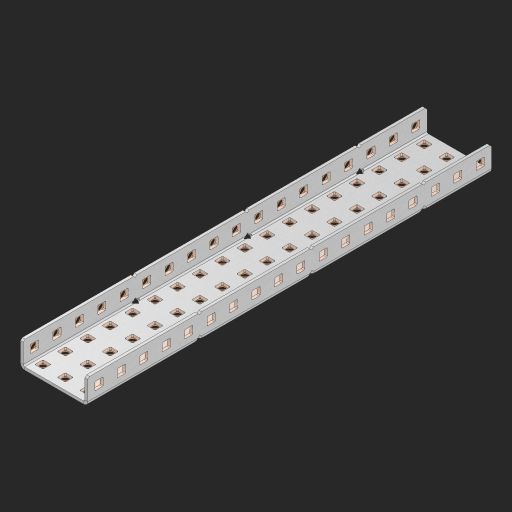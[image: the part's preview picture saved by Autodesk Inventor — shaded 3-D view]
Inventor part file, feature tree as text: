
AUTODESK INVENTOR PART (.ipt)
format: ipt  version: 2023 (Build 270158000, 158)  size: 1,276,928 bytes
history: native  units: in
note: dims shown in document units (in); Inventor stores cm internally (conversion verified against a paired STEP export)
features: other x95, extrude x89, sheet_metal_op x10, sketch x8, mirror x1, pattern_linear x1, chamfer x1
ambient origin geometry x8: Origin, YZ Plane, XZ Plane, XY Plane, X Axis, Y Axis, Z Axis, Center Point
bodies: Solid1 (feature_tree), Body (feature_tree)
feature tree (205):
  other  "Flange Pattern Plane"
  sheet_metal_op  "Flange Pattern"
  sheet_metal_op  "Body Pattern"
  other  "Arc Length"
  mirror  "Notch Mirror"
  pattern_linear  "Notch Pattern"  Spacing1=0.25in  [1 undecoded]
  chamfer  "End Chamfer"
  extrude  "Half Cut"  Depth=0.0625in
  sketch  "Sketch1"  dims[d0=1.5in]
  other  "Plate1"
  sketch  "Sketch2"  dims[d1=9.0in]
  other  "Plate2"
  sheet_metal_op  "Bend1"
  sheet_metal_op  "Corner1"
  sketch  "Sketch3"  dims[d2=0.0625in]
  other  "Flange Pattern Sketch"
  sketch  "Sketch7"  dims[d3=0.0625in]
  other  "Srf1"
  other  "Srf2"
  sketch  "Sketch8"  dims[d4=0.0312in]
  sketch  "Sketch9"  dims[d5=0.125in]
  other  "Srf91"
  sheet_metal_op  "Body Pattern Sketch"
  other  "Srf92"
  sketch  "Sketch13"  dims[d6=0.0625in]
  sketch  "Sketch14"  dims[d7=0.5in d8=90.0deg d9=0.0312in d10=0.25in d11=0.0625in d12=0.0625in d16=0.182in d17=0.02in d18=0.0625in d19=0.0in d20=0.25in d21=0.25in d46=0.172in d47=1.0in d48=0.0in d49=0.182in d50=0.02in d51=0.25in d52=0.25in d53=0.0625in d54=0.0in d55=0.172in d56=1.0in d57=0.0in d60=7.0866in d62=0.5in d63=1.1811in d65=0.5in d85=0.1473in d86=0.1782in d88=0.04in d89=0.0625in d90=0.0in d91=0.04in d92=0.0491in d95=2.5in d96=0.04in d97=0.25in d98=45.0deg d101=0.0in d102=2.497in d131=1.5in d132=7.0866in d134=0.5in d139=0.5in]
  other  "Srf856"
  other  "Srf1310"
  other  "Srf1311"
  other  "Srf1312"
  other  "Srf1376"
  other  "Srf1377"
  other  "Srf1728"
  other  "Srf1755"
  other  "Srf1878"
  other  "Srf1879"
  other  "Srf1880"
  other  "Srf1881"
  other  "Srf1882"
  other  "Srf1883"
  other  "Srf1884"
  other  "Srf1885"
  other  "Srf1886"
  other  "Srf1887"
  other  "Srf1888"
  other  "Srf1889"
  other  "Srf1890"
  other  "Srf1891"
  other  "Srf1892"
  other  "Srf1893"
  other  "Srf1894"
  other  "Srf1895"
  other  "Srf1896"
  other  "Srf1897"
  other  "Srf1898"
  other  "Srf1899"
  other  "Srf1900"
  other  "Srf1901"
  other  "Srf1902"
  other  "Srf1903"
  other  "Srf1904"
  other  "Srf1905"
  other  "Srf1906"
  other  "Srf1907"
  other  "Srf1942"
  other  "Srf1943"
  other  "Srf1944"
  other  "Srf1945"
  other  "Srf1946"
  other  "Srf1947"
  other  "Srf1948"
  other  "Srf1949"
  other  "Srf1950"
  other  "Srf1951"
  other  "Srf1952"
  other  "Srf1953"
  other  "Srf1954"
  other  "Srf1955"
  other  "Srf1956"
  other  "Srf1957"
  other  "Srf1958"
  other  "Srf1959"
  other  "Srf1960"
  other  "Srf1961"
  other  "Srf1962"
  other  "Srf1963"
  other  "Srf1964"
  other  "Srf1965"
  other  "Srf1966"
  other  "Srf1967"
  other  "Srf1968"
  other  "Srf1969"
  other  "Srf1970"
  other  "Srf1971"
  other  "Srf1972"
  other  "Srf1973"
  other  "Srf1974"
  other  "Srf1975"
  other  "Srf1976"
  other  "Srf1977"
  other  "Srf1978"
  other  "Srf1979"
  other  "Srf1980"
  other  "Srf1981"
  other  "Srf1982"
  other  "Srf1983"
  other  "Srf1984"
  other  "Srf1985"
  other  "Srf1986"
  other  "Srf1987"
  other  "Srf1988"
  other  "Srf1989"
  sheet_metal_op  "Flange Stamp"
  sheet_metal_op  "Flange Circle"
  sheet_metal_op  "Body Stamp"
  sheet_metal_op  "Body Circle"
  sheet_metal_op  "Notch"
  extrude  "ExtrusionSrf2"  Depth=0.0625in
  extrude  "ExtrusionSrf92"  Depth=1.5in
  extrude  "ExtrusionSrf856"  Depth=0.02in
  extrude  "ExtrusionSrf1310"  Depth=0.0625in
  extrude  "ExtrusionSrf1311"  TaperAngle=0.0deg  [1 undecoded]
  extrude  "ExtrusionSrf1312"  Depth=0.25in
  extrude  "ExtrusionSrf1376"  Depth=0.25in
  extrude  "ExtrusionSrf1377"  Depth=1.5in
  extrude  "ExtrusionSrf1728"  Depth=1.5in TaperAngle=0.0deg
  extrude  "ExtrusionSrf1755"  Depth=1.5in
  extrude  "ExtrusionSrf1878"  Depth=0.02in
  extrude  "ExtrusionSrf1879"  Depth=0.25in
  extrude  "ExtrusionSrf1880"  Depth=0.25in
  extrude  "ExtrusionSrf1881"  Depth=0.0625in
  extrude  "ExtrusionSrf1882"  TaperAngle=0.0deg  [1 undecoded]
  extrude  "ExtrusionSrf1883"  Depth=1.5in
  extrude  "ExtrusionSrf1884"  Depth=1.5in TaperAngle=0.0deg
  extrude  "ExtrusionSrf1885"  Depth=1.5in
  extrude  "ExtrusionSrf1886"  Depth=1.5in
  extrude  "ExtrusionSrf1887"  Depth=1.5in
  extrude  "ExtrusionSrf1888"  Depth=1.5in
  extrude  "ExtrusionSrf1889"  Depth=1.5in
  extrude  "ExtrusionSrf1890"  Depth=0.0625in
  extrude  "ExtrusionSrf1891"  TaperAngle=0.0deg  [1 undecoded]
  extrude  "ExtrusionSrf1892"  Depth=1.5in
  extrude  "ExtrusionSrf1893"  Depth=1.5in
  extrude  "ExtrusionSrf1894"  Depth=1.5in
  extrude  "ExtrusionSrf1895"  Depth=0.25in TaperAngle=45.0deg
  extrude  "ExtrusionSrf1896"  TaperAngle=0.0deg  [1 undecoded]
  extrude  "ExtrusionSrf1897"  Depth=1.5in
  extrude  "ExtrusionSrf1898"  Depth=1.5in
  extrude  "ExtrusionSrf1899"  Depth=1.5in
  extrude  "ExtrusionSrf1900"  Depth=1.5in
  extrude  "ExtrusionSrf1901"  Depth=1.5in
  extrude  "ExtrusionSrf1902"  [1 undecoded]
  extrude  "ExtrusionSrf1903"  [1 undecoded]
  extrude  "ExtrusionSrf1904"  [1 undecoded]
  extrude  "ExtrusionSrf1905"  [1 undecoded]
  extrude  "ExtrusionSrf1906"  [1 undecoded]
  extrude  "ExtrusionSrf1907"  [1 undecoded]
  extrude  "ExtrusionSrf1942"  [1 undecoded]
  extrude  "ExtrusionSrf1943"  [1 undecoded]
  extrude  "ExtrusionSrf1944"  [1 undecoded]
  extrude  "ExtrusionSrf1945"  [1 undecoded]
  extrude  "ExtrusionSrf1946"  [1 undecoded]
  extrude  "ExtrusionSrf1947"  [1 undecoded]
  extrude  "ExtrusionSrf1948"  [1 undecoded]
  extrude  "ExtrusionSrf1949"  [1 undecoded]
  extrude  "ExtrusionSrf1950"  [1 undecoded]
  extrude  "ExtrusionSrf1951"  [1 undecoded]
  extrude  "ExtrusionSrf1952"  [1 undecoded]
  extrude  "ExtrusionSrf1953"  [1 undecoded]
  extrude  "ExtrusionSrf1954"  [1 undecoded]
  extrude  "ExtrusionSrf1955"  [1 undecoded]
  extrude  "ExtrusionSrf1956"  [1 undecoded]
  extrude  "ExtrusionSrf1957"  [1 undecoded]
  extrude  "ExtrusionSrf1958"  [1 undecoded]
  extrude  "ExtrusionSrf1959"  [1 undecoded]
  extrude  "ExtrusionSrf1960"  [1 undecoded]
  extrude  "ExtrusionSrf1961"  [1 undecoded]
  extrude  "ExtrusionSrf1962"  [1 undecoded]
  extrude  "ExtrusionSrf1963"  [1 undecoded]
  extrude  "ExtrusionSrf1964"  [1 undecoded]
  extrude  "ExtrusionSrf1965"  [1 undecoded]
  extrude  "ExtrusionSrf1966"  [1 undecoded]
  extrude  "ExtrusionSrf1967"  [1 undecoded]
  extrude  "ExtrusionSrf1968"  [1 undecoded]
  extrude  "ExtrusionSrf1969"  [1 undecoded]
  extrude  "ExtrusionSrf1970"  [1 undecoded]
  extrude  "ExtrusionSrf1971"  [1 undecoded]
  extrude  "ExtrusionSrf1972"  [1 undecoded]
  extrude  "ExtrusionSrf1973"  [1 undecoded]
  extrude  "ExtrusionSrf1974"  [1 undecoded]
  extrude  "ExtrusionSrf1975"  [1 undecoded]
  extrude  "ExtrusionSrf1976"  [1 undecoded]
  extrude  "ExtrusionSrf1977"  [1 undecoded]
  extrude  "ExtrusionSrf1978"  [1 undecoded]
  extrude  "ExtrusionSrf1979"  [1 undecoded]
  extrude  "ExtrusionSrf1980"  [1 undecoded]
  extrude  "ExtrusionSrf1981"  [1 undecoded]
  extrude  "ExtrusionSrf1982"  [1 undecoded]
  extrude  "ExtrusionSrf1983"  [1 undecoded]
  extrude  "ExtrusionSrf1984"  [1 undecoded]
  extrude  "ExtrusionSrf1985"  [1 undecoded]
  extrude  "ExtrusionSrf1986"  [1 undecoded]
  extrude  "ExtrusionSrf1987"  [1 undecoded]
  extrude  "ExtrusionSrf1988"  [1 undecoded]
  extrude  "ExtrusionSrf1989"  [1 undecoded]
note: 59 required parameter values undecoded (feature->parameter linkage not recoverable at this tier; creation-order binding heuristic only, values carry confidence <= 0.55)
